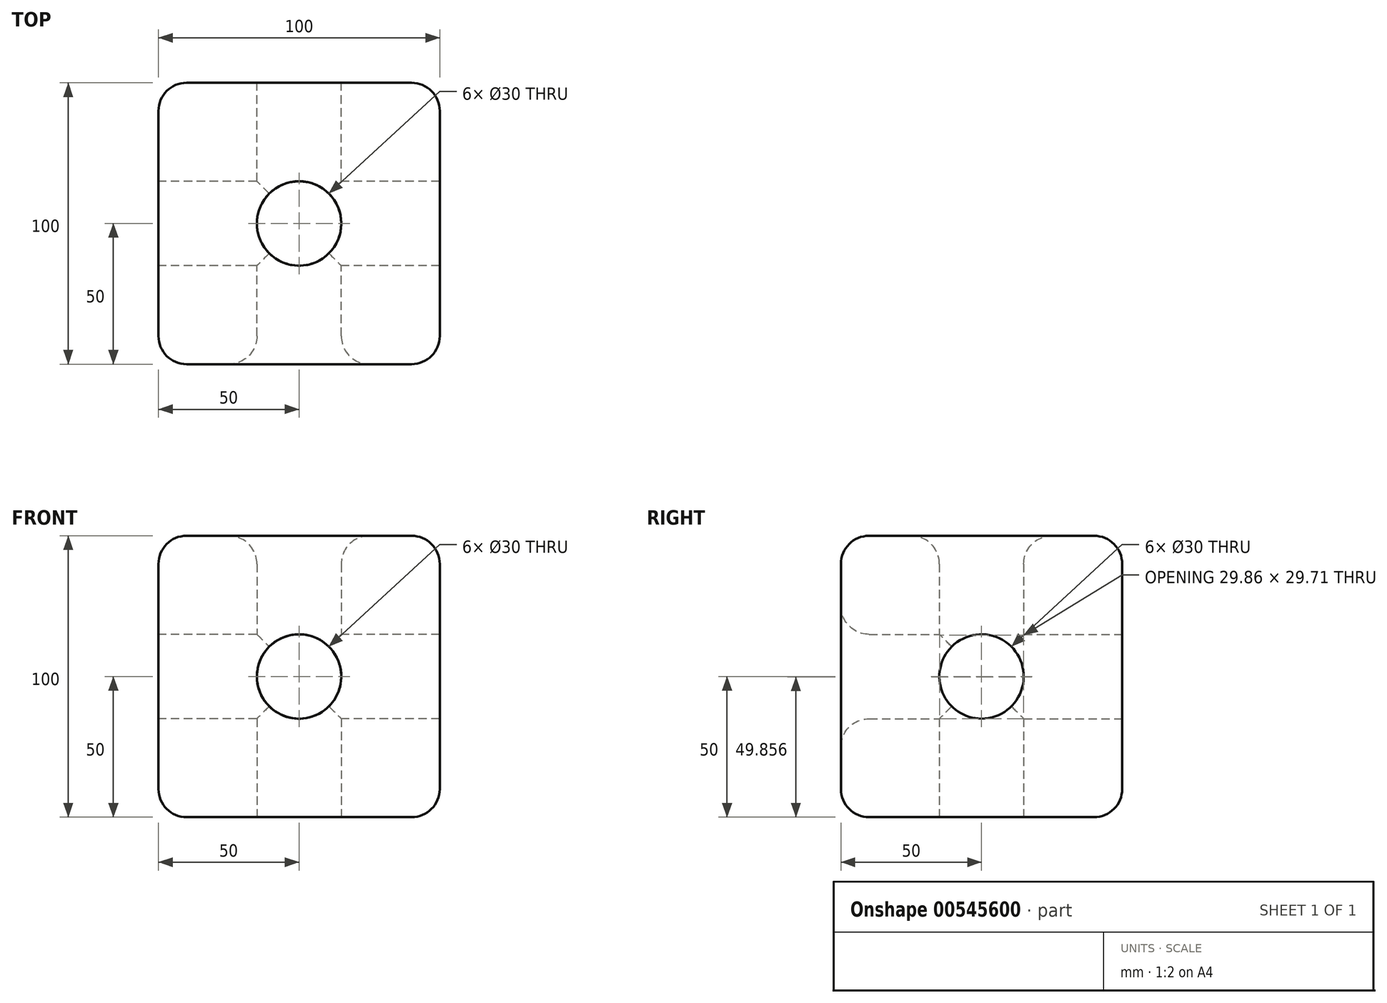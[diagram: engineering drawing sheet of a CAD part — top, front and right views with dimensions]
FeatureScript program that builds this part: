
annotation { "Feature Type Name" : "Feature", "Feature Type Description" : "" }
export const myFeature = defineFeature(function(context is Context, id is Id, definition is map)
    precondition{}
    {
        {
            var Q0;
            Q0=qCreatedBy(makeId("Front.planeOp"),FACE);
            var sketch = newSketch(context, id + "F0", { "sketchPlane" : qUnion([Q0])});
            skLineSegment(sketch, "E0.bottom", {"start": v(-50, 50) * mm, "end": v(50, 50) * mm});
            skLineSegment(sketch, "E0.top", {"start": v(-50, -50) * mm, "end": v(50, -50) * mm});
            skLineSegment(sketch, "E0.left", {"start": v(-50, 50) * mm, "end": v(-50, -50) * mm});
            skLineSegment(sketch, "E0.right", {"start": v(50, 50) * mm, "end": v(50, -50) * mm});
            skSolve(sketch);
        }
        {
            var Q0;
            Q0 = qSketchRegion(id + "F0", true);
            extrude(context, id + "F1", {"entities" : qUnion([Q0]), "endBound" : BoundingType.SYMMETRIC, "depth" : 100 * mm, "offsetDistance" : 25 * mm});
        }
        {
            var Q0;
            Q0=makeQuery(id+"F1.opExtrude","SWEPT_FACE",FACE,{"disambiguationData":[OSD([sQuery(id+"F0.wireOp",EDGE,"E0.left")])]});
            var sketch = newSketch(context, id + "F2", { "sketchPlane" : qUnion([Q0])});
            skCircle(sketch, "E1", {"center": v(0, 0) * mm, "radius": 15 * mm});
            skSolve(sketch);
        }
        {
            var Q0;
            Q0=makeQuery(id+"F2.imprint","IMPRINT",FACE,{"disambiguationData":[TD([[makeQuery(id+"F2.imprint","IMPRINT",EDGE,{"derivedFrom":sQuery(id+"F2.wireOp",EDGE,"E1")}),1.0]])]});
            extrude(context, id + "F3", {"entities" : qUnion([Q0]), "operationType" : NewBodyOperationType.REMOVE, "endBound" : BoundingType.UP_TO_NEXT, "oppositeDirection" : true, "depth" : 25 * mm, "offsetDistance" : 25 * mm});
        }
        {
            var Q0;
            Q0=makeQuery(id+"F1.opExtrude","CAP_FACE",FACE,{"disambiguationData":[OSD([sQuery(id+"F0.wireOp",EDGE,"E0.bottom"),sQuery(id+"F0.wireOp",EDGE,"E0.top"),sQuery(id+"F0.wireOp",EDGE,"E0.left"),sQuery(id+"F0.wireOp",EDGE,"E0.right")])],"isStart":true});
            var sketch = newSketch(context, id + "F4", { "sketchPlane" : qUnion([Q0])});
            skCircle(sketch, "E2", {"center": v(0, 0) * mm, "radius": 15 * mm});
            skSolve(sketch);
        }
        {
            var Q0;
            Q0=makeQuery(id+"F4.imprint","IMPRINT",FACE,{"disambiguationData":[TD([[makeQuery(id+"F4.imprint","IMPRINT",EDGE,{"derivedFrom":sQuery(id+"F4.wireOp",EDGE,"E2")}),1.0]])]});
            extrude(context, id + "F5", {"entities" : qUnion([Q0]), "operationType" : NewBodyOperationType.REMOVE, "endBound" : BoundingType.THROUGH_ALL, "oppositeDirection" : true, "depth" : 25 * mm, "offsetDistance" : 25 * mm});
        }
        {
            var Q0;
            Q0=makeQuery(id+"F1.opExtrude","SWEPT_FACE",FACE,{"disambiguationData":[OSD([sQuery(id+"F0.wireOp",EDGE,"E0.top")])]});
            var sketch = newSketch(context, id + "F6", { "sketchPlane" : qUnion([Q0])});
            skCircle(sketch, "E3", {"center": v(0, 0) * mm, "radius": 15 * mm});
            skSolve(sketch);
        }
        {
            var Q0;
            Q0=makeQuery(id+"F6.imprint","IMPRINT",FACE,{"disambiguationData":[TD([[makeQuery(id+"F6.imprint","IMPRINT",EDGE,{"derivedFrom":sQuery(id+"F6.wireOp",EDGE,"E3")}),1.0]])]});
            extrude(context, id + "F7", {"entities" : qUnion([Q0]), "operationType" : NewBodyOperationType.REMOVE, "endBound" : BoundingType.THROUGH_ALL, "oppositeDirection" : true, "depth" : 25 * mm, "offsetDistance" : 25 * mm});
        }
        {
            var Q0;
            Q0=makeQuery(id+"F1.opExtrude","SWEPT_EDGE",EDGE,{"disambiguationData":[OSD([sQuery(id+"F0.wireOp",EDGE,"E0.bottom"),sQuery(id+"F0.wireOp",EDGE,"E0.right")])]});
            var Q1;
            Q1=makeQuery(id+"F1.opExtrude","CAP_EDGE",EDGE,{"disambiguationData":[OSD([sQuery(id+"F0.wireOp",EDGE,"E0.bottom")])],"isStart":true});
            var Q2;
            Q2=makeQuery(id+"F1.opExtrude","SWEPT_EDGE",EDGE,{"disambiguationData":[OSD([sQuery(id+"F0.wireOp",EDGE,"E0.bottom"),sQuery(id+"F0.wireOp",EDGE,"E0.left")])]});
            var Q3;
            Q3=makeQuery(id+"F1.opExtrude","CAP_EDGE",EDGE,{"disambiguationData":[OSD([sQuery(id+"F0.wireOp",EDGE,"E0.bottom")])],"isStart":false});
            var Q4;
            Q4=makeQuery(id+"F1.opExtrude","CAP_EDGE",EDGE,{"disambiguationData":[OSD([sQuery(id+"F0.wireOp",EDGE,"E0.right")])],"isStart":true});
            var Q5;
            Q5=makeQuery(id+"F1.opExtrude","CAP_EDGE",EDGE,{"disambiguationData":[OSD([sQuery(id+"F0.wireOp",EDGE,"E0.left")])],"isStart":true});
            var Q6;
            Q6=makeQuery(id+"F1.opExtrude","CAP_EDGE",EDGE,{"disambiguationData":[OSD([sQuery(id+"F0.wireOp",EDGE,"E0.top")])],"isStart":true});
            var Q7;
            Q7=makeQuery(id+"F1.opExtrude","SWEPT_EDGE",EDGE,{"disambiguationData":[OSD([sQuery(id+"F0.wireOp",EDGE,"E0.top"),sQuery(id+"F0.wireOp",EDGE,"E0.right")])]});
            var Q8;
            Q8=makeQuery(id+"F1.opExtrude","CAP_EDGE",EDGE,{"disambiguationData":[OSD([sQuery(id+"F0.wireOp",EDGE,"E0.right")])],"isStart":false});
            var Q9;
            Q9=makeQuery(id+"F1.opExtrude","CAP_EDGE",EDGE,{"disambiguationData":[OSD([sQuery(id+"F0.wireOp",EDGE,"E0.left")])],"isStart":false});
            var Q10;
            Q10=makeQuery(id+"F1.opExtrude","SWEPT_EDGE",EDGE,{"disambiguationData":[OSD([sQuery(id+"F0.wireOp",EDGE,"E0.top"),sQuery(id+"F0.wireOp",EDGE,"E0.left")])]});
            var Q11;
            Q11=makeQuery(id+"F1.opExtrude","CAP_EDGE",EDGE,{"disambiguationData":[OSD([sQuery(id+"F0.wireOp",EDGE,"E0.top")])],"isStart":false});
            fillet(context, id + "F8", {"entities" : qUnion([Q0, Q1, Q2, Q3, Q4, Q5, Q6, Q7, Q8, Q9, Q10, Q11]), "radius" : 10 * mm, "tangentPropagation" : true, "allowEdgeOverflow" : false});
        }
        {
            var Q0;
            Q0=makeQuery(id+"F7.boolean.opBoolean","INTERSECT",EDGE,{"derivedFrom":[makeQuery(id+"F1.opExtrude","SWEPT_FACE",FACE,{"disambiguationData":[OSD([sQuery(id+"F0.wireOp",EDGE,"E0.bottom")])]}),makeQuery(id+"F7.opExtrude","SWEPT_FACE",FACE,{"disambiguationData":[OSD([sQuery(id+"F6.wireOp",EDGE,"E3")])]})]});
            var Q1;
            Q1=makeQuery(id+"F5.boolean.opBoolean","COPY",EDGE,{"derivedFrom":makeQuery(id+"F5.opExtrude","CAP_EDGE",EDGE,{"disambiguationData":[OSD([sQuery(id+"F4.wireOp",EDGE,"E2")])],"isStart":true})});
            var Q2;
            Q2=makeQuery(id+"F3.boolean.opBoolean","COPY",EDGE,{"derivedFrom":makeQuery(id+"F3.opExtrude","CAP_EDGE",EDGE,{"disambiguationData":[OSD([sQuery(id+"F2.wireOp",EDGE,"E1")])],"isStart":false})});
            var Q3;
            Q3=makeQuery(id+"F3.boolean.opBoolean","COPY",EDGE,{"derivedFrom":makeQuery(id+"F3.opExtrude","CAP_EDGE",EDGE,{"disambiguationData":[OSD([sQuery(id+"F2.wireOp",EDGE,"E1")])],"isStart":true})});
            var Q4;
            Q4=makeQuery(id+"F5.boolean.opBoolean","INTERSECT",EDGE,{"derivedFrom":[makeQuery(id+"F1.opExtrude","CAP_FACE",FACE,{"disambiguationData":[OSD([sQuery(id+"F0.wireOp",EDGE,"E0.bottom"),sQuery(id+"F0.wireOp",EDGE,"E0.top"),sQuery(id+"F0.wireOp",EDGE,"E0.left"),sQuery(id+"F0.wireOp",EDGE,"E0.right")])],"isStart":false}),makeQuery(id+"F5.opExtrude","SWEPT_FACE",FACE,{"disambiguationData":[OSD([sQuery(id+"F4.wireOp",EDGE,"E2")])]})]});
            var Q5;
            Q5=makeQuery(id+"F7.boolean.opBoolean","COPY",EDGE,{"derivedFrom":makeQuery(id+"F7.opExtrude","CAP_EDGE",EDGE,{"disambiguationData":[OSD([sQuery(id+"F6.wireOp",EDGE,"E3")])],"isStart":true})});
            fillet(context, id + "F9", {"entities" : qUnion([Q0, Q1, Q2, Q3, Q4, Q5]), "radius" : 10 * mm, "tangentPropagation" : true, "allowEdgeOverflow" : false});
        }
    });
